# Revit family: IS_ConnectSpace_E0380_BIM_DE
name_source: partatom
category: Plumbing Fixtures
revit_build: Autodesk Revit MEP 2016 (Build: 20161004_0715(x64)
units: mm (PartAtom-declared; Revit-internal decimal feet)

## family parameters
Always vertical = No
Cut with Voids When Loaded = No
Part Type = Normal
Room Calculation Point = No
Round Connector Dimension = Use Diameter
Shared = No
Work Plane-Based = No

## types (1)
- E0380BH CONNECT mirror 400x20mm
    Accessories = www.idealstandard.de\ersatzteile
    Assembly Code = C1030200
    AssetType = Fest
    BIMobject category = Mirrors
    BOSUseNativeGeometries = 1
    BarCode = 5017830455530
    Brand = Ideal Standard
    Brand url = http://www.idealstandard.de
    Color = Mirrored
    Cost = 0 $
    CurrencyUnit = €
    CurrentRevision = 1
    Date of publishing = 15/09/2017
    Description = E0380BH CONNECT mirror 400x20mm
    DurationUnit = Jahr
    EAN code = https://5017830455530
    Edition number = 1
    ExpectedLife = 25
    Features = CONNECT mirror 400x20mm
    Finish = Mirrored
    IFC Classification = Sanitary Terminal
    Installation instructions = http://www.idealstandard.de
    InstallationInstructions = www.idealstandard.de\produkte
    MainColor = Mirrored
    Manufacturer = www.idealstandard.de\produkte
    Manufacturer name = Ideal Standard
    ManufacturerURL = http://www.idealstandard.de
    Material = glass
    Material main = Glass
    Model = E0380BH
    ModelNumber = E0380BH
    ModelReference = E0380BH CONNECT mirror 400x20mm
    NettWeight = 4 kg
    Nominal height = 0
    Nominal width = 0
    NominalHeight = 700 mm  [stored 2.29659 ft]
    NominalLength = 20 mm
    NominalWidth = 400 mm  [stored 1.31234 ft]
    Product Guid = c744f60b-07c7-4904-9023-4e614214e3fc
    Product SKU = E0380
    Product data url = https://bimobject.com
    Product family = CONNECT SPACE
    Product group = Mirror
    Product name = CONNECT SPACE mirror 400x20mm
    Product url = http://www.idealstandard.de
    ProductInformation = www.idealstandard.de\produkte
    QR code = http://bimobject.com
    Shape = Rectangular
    Size = 700x20x400 mm
    Space = Intern
    SpareParts = www.idealstandard.de/ersatzteile
    Technical description = http://www.idealstandard.de
    URL = http://www.idealstandard.de
    Uniclass2015Code = Pr_25_71_53_06
    Uniclass2015Title = Bathroom mirrors
    Uniclass2015Version = Products v1.1
    Version = 1
    VolumeUnits = Litres
    Weight Net (Kg) = 4

note: [stored X ft] marks values corroborated as IEEE doubles in the binary element streams (Revit-internal decimal feet)

## geometry (parser evidence)
native form markers: Blend x4, Sweep x1
no freeform markers — native parametric forms only
